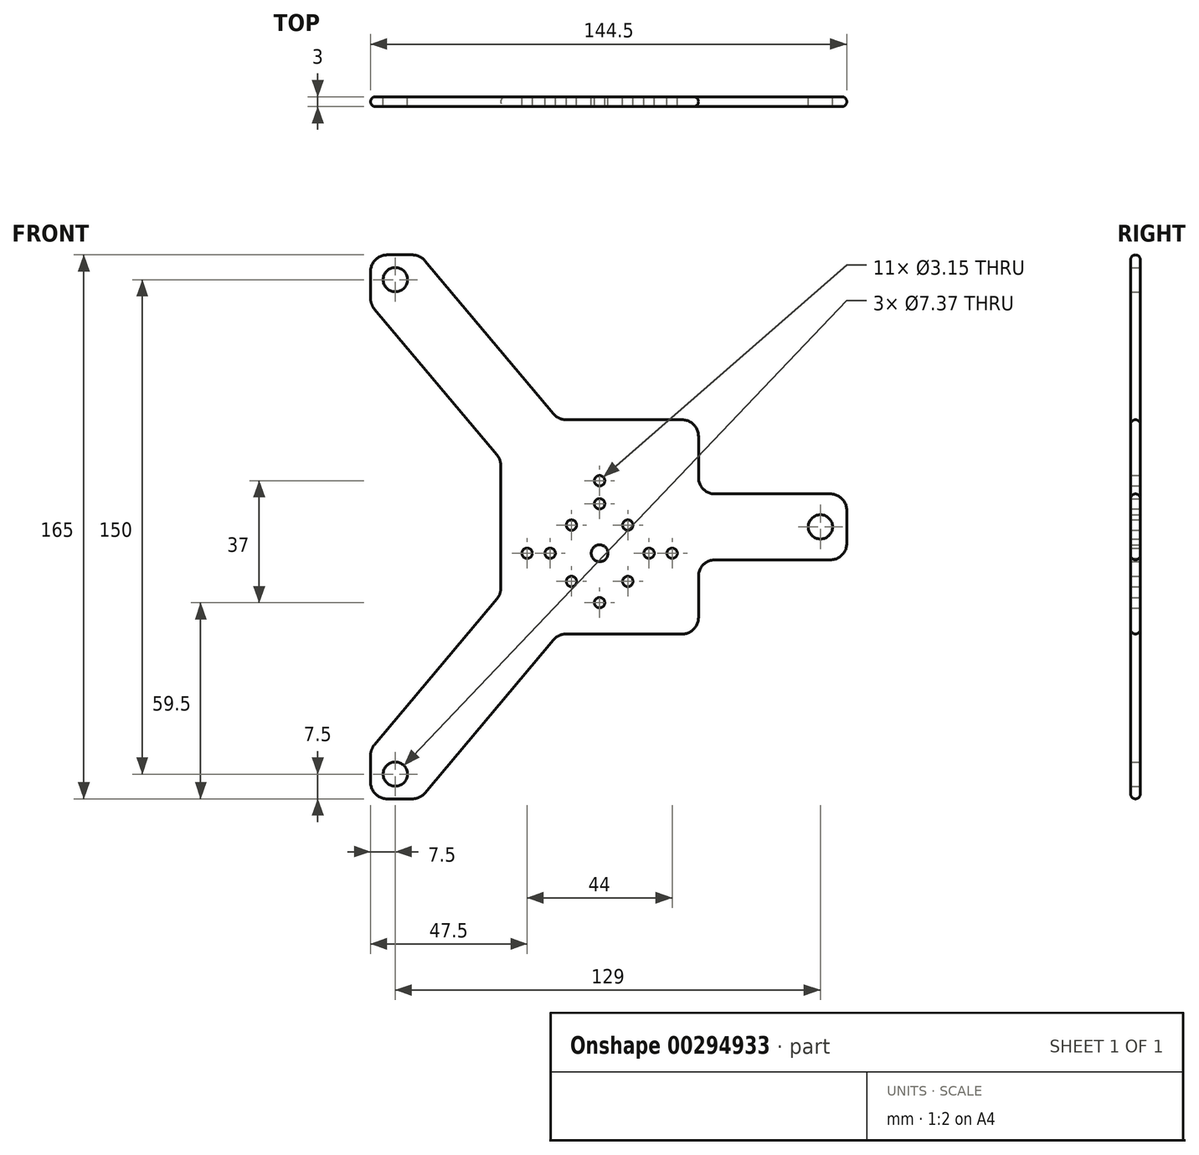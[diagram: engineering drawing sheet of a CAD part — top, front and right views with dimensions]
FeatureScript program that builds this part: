
annotation { "Feature Type Name" : "Feature", "Feature Type Description" : "" }
export const myFeature = defineFeature(function(context is Context, id is Id, definition is map)
    precondition{}
    {
        {
            var Q0;
            Q0=qCreatedBy(makeId("Front.planeOp"),FACE);
            var sketch = newSketch(context, id + "F0", { "sketchPlane" : qUnion([Q0])});
            skPoint(sketch, "E0.middle", {"position": v(0, 0) * mm});
            skCircle(sketch, "E1", {"center": v(0, -8) * mm, "radius": 2.55 * mm});
            skCircle(sketch, "E2", {"center": v(0, 7) * mm, "radius": 1.57 * mm});
            skCircle(sketch, "E3", {"center": v(0, 14) * mm, "radius": 1.57 * mm});
            skCircle(sketch, "E4", {"center": v(15, -8) * mm, "radius": 1.57 * mm});
            skCircle(sketch, "E5", {"center": v(22, -8) * mm, "radius": 1.57 * mm});
            skCircle(sketch, "E6", {"center": v(8.55, 0.55) * mm, "radius": 1.57 * mm});
            skCircle(sketch, "E7.MirrorC", {"center": v(-8.55, 0.55) * mm, "radius": 1.57 * mm});
            skCircle(sketch, "E8.MirrorC", {"center": v(-15, -8) * mm, "radius": 1.57 * mm});
            skCircle(sketch, "E9.MirrorC", {"center": v(-22, -8) * mm, "radius": 1.57 * mm});
            skCircle(sketch, "E10.MirrorC", {"center": v(8.55, -16.55) * mm, "radius": 1.57 * mm});
            skCircle(sketch, "E11.MirrorC", {"center": v(-8.55, -16.55) * mm, "radius": 1.57 * mm});
            skCircle(sketch, "E12.MirrorC", {"center": v(0, -23) * mm, "radius": 1.57 * mm});
            skCircle(sketch, "E13", {"center": v(-62, 75) * mm, "radius": 3.68 * mm});
            skCircle(sketch, "E14", {"center": v(-62, -75) * mm, "radius": 3.68 * mm});
            skLineSegment(sketch, "E15.bottom", {"start": v(-56.83, -82.5) * mm, "end": v(-64.5, -82.5) * mm});
            skLineSegment(sketch, "E15.top", {"start": v(-56.83, 82.5) * mm, "end": v(-64.5, 82.5) * mm});
            skLineSegment(sketch, "E15.left", {"start": v(75, -5) * mm, "end": v(75, 5) * mm});
            skLineSegment(sketch, "E15.right", {"start": v(-69.5, -77.5) * mm, "end": v(-69.5, -69.32) * mm});
            skLineSegment(sketch, "E16.bottom", {"start": v(25, -32.5) * mm, "end": v(-10.21, -32.5) * mm});
            skLineSegment(sketch, "E16.top", {"start": v(25, 32.5) * mm, "end": v(-10.21, 32.5) * mm});
            skLineSegment(sketch, "E16.left", {"start": v(30, -27.5) * mm, "end": v(30, -15) * mm});
            skLineSegment(sketch, "E16.right", {"start": v(-30, -18.6) * mm, "end": v(-30, 18.6) * mm});
            skCircle(sketch, "E17", {"center": v(67, 0) * mm, "radius": 3.68 * mm});
            skLineSegment(sketch, "E18", {"start": v(35, 10) * mm, "end": v(70, 10) * mm});
            skLineSegment(sketch, "E19.MirrorCS", {"start": v(35, -10) * mm, "end": v(70, -10) * mm});
            skLineSegment(sketch, "E20", {"start": v(-68.33, 66.1) * mm, "end": v(-31.17, 21.82) * mm});
            skLineSegment(sketch, "E21", {"start": v(-53, 80.71) * mm, "end": v(-14.04, 34.29) * mm});
            skLineSegment(sketch, "E22.MirrorCS", {"start": v(-68.33, -66.1) * mm, "end": v(-31.17, -21.82) * mm});
            skLineSegment(sketch, "E23.MirrorCS", {"start": v(-53, -80.71) * mm, "end": v(-14.04, -34.29) * mm});
            skLineSegment(sketch, "E24.trimOffspring", {"start": v(-69.5, 69.32) * mm, "end": v(-69.5, 77.5) * mm});
            skPoint(sketch, "E25.MirrorCS.start.orphan", {"position": v(-69.5, -67.5) * mm});
            skPoint(sketch, "E26.MirrorCS.end.orphan", {"position": v(-54.5, -82.5) * mm});
            skLineSegment(sketch, "E27.trimOffspring", {"start": v(30, 15) * mm, "end": v(30, 27.5) * mm});
            skPoint(sketch, "E28.orphan", {"position": v(30, 0) * mm});
            skPoint(sketch, "E29.orphan", {"position": v(69.5, 0) * mm});
            skPoint(sketch, "E30.visualSharp", {"position": v(-12.55, 32.5) * mm});
            skArc(sketch, "E30.filletArc", {"start": v(-14.04, 34.29) * mm, "mid": v(-12.33, 32.97) * mm, "end": v(-10.21, 32.5) * mm});
            skPoint(sketch, "E31.visualSharp", {"position": v(-30, 20.43) * mm});
            skArc(sketch, "E31.filletArc", {"start": v(-30, 18.6) * mm, "mid": v(-30.3, 20.32) * mm, "end": v(-31.17, 21.82) * mm});
            skPoint(sketch, "E32.visualSharp", {"position": v(-30, -20.43) * mm});
            skArc(sketch, "E32.filletArc", {"start": v(-31.17, -21.82) * mm, "mid": v(-30.3, -20.32) * mm, "end": v(-30, -18.6) * mm});
            skPoint(sketch, "E33.visualSharp", {"position": v(-12.55, -32.5) * mm});
            skArc(sketch, "E33.filletArc", {"start": v(-10.21, -32.5) * mm, "mid": v(-12.33, -32.97) * mm, "end": v(-14.04, -34.29) * mm});
            skPoint(sketch, "E34.visualSharp", {"position": v(30, -32.5) * mm});
            skArc(sketch, "E34.filletArc", {"start": v(25, -32.5) * mm, "mid": v(28.54, -31.04) * mm, "end": v(30, -27.5) * mm});
            skPoint(sketch, "E35.visualSharp", {"position": v(30, -10) * mm});
            skArc(sketch, "E35.filletArc", {"start": v(35, -10) * mm, "mid": v(31.46, -11.46) * mm, "end": v(30, -15) * mm});
            skPoint(sketch, "E36.visualSharp", {"position": v(30, 10) * mm});
            skArc(sketch, "E36.filletArc", {"start": v(30, 15) * mm, "mid": v(31.46, 11.46) * mm, "end": v(35, 10) * mm});
            skPoint(sketch, "E37.visualSharp", {"position": v(30, 32.5) * mm});
            skArc(sketch, "E37.filletArc", {"start": v(30, 27.5) * mm, "mid": v(28.54, 31.04) * mm, "end": v(25, 32.5) * mm});
            skPoint(sketch, "E38.visualSharp", {"position": v(75, 10) * mm});
            skArc(sketch, "E38.filletArc", {"start": v(75, 5) * mm, "mid": v(73.54, 8.54) * mm, "end": v(70, 10) * mm});
            skPoint(sketch, "E39.visualSharp", {"position": v(75, -10) * mm});
            skArc(sketch, "E39.filletArc", {"start": v(70, -10) * mm, "mid": v(73.54, -8.54) * mm, "end": v(75, -5) * mm});
            skArc(sketch, "E40.filletArc", {"start": v(-56.83, -82.5) * mm, "mid": v(-54.72, -82.03) * mm, "end": v(-53, -80.71) * mm});
            skPoint(sketch, "E41.visualSharp", {"position": v(-69.5, -82.5) * mm});
            skArc(sketch, "E41.filletArc", {"start": v(-69.5, -77.5) * mm, "mid": v(-68.04, -81.04) * mm, "end": v(-64.5, -82.5) * mm});
            skArc(sketch, "E42.filletArc", {"start": v(-68.33, -66.1) * mm, "mid": v(-69.2, -67.6) * mm, "end": v(-69.5, -69.32) * mm});
            skPoint(sketch, "E43.visualSharp", {"position": v(-69.5, 67.5) * mm});
            skArc(sketch, "E43.filletArc", {"start": v(-69.5, 69.32) * mm, "mid": v(-69.2, 67.6) * mm, "end": v(-68.33, 66.1) * mm});
            skPoint(sketch, "E44.visualSharp", {"position": v(-69.5, 82.5) * mm});
            skArc(sketch, "E44.filletArc", {"start": v(-64.5, 82.5) * mm, "mid": v(-68.04, 81.04) * mm, "end": v(-69.5, 77.5) * mm});
            skPoint(sketch, "E45.visualSharp", {"position": v(-54.5, 82.5) * mm});
            skArc(sketch, "E45.filletArc", {"start": v(-53, 80.71) * mm, "mid": v(-54.72, 82.03) * mm, "end": v(-56.83, 82.5) * mm});
            skSolve(sketch);
        }
        {
            var Q0;
            Q0=makeQuery(id+"F0.imprint","IMPRINT",FACE,{"disambiguationData":[TD([[makeQuery(id+"F0.imprint","IMPRINT",EDGE,{"derivedFrom":sQuery(id+"F0.wireOp",EDGE,"E1")}),-1.0]])]});
            extrude(context, id + "F1", {"entities" : qUnion([Q0]), "depth" : 3 * mm});
        }
        {
            var Q0;
            Q0=makeQuery(id+"F1.opExtrude","CAP_EDGE",EDGE,{"disambiguationData":[OSD([sQuery(id+"F0.wireOp",EDGE,"E21")])],"isStart":false});
            var Q1;
            Q1=makeQuery(id+"F1.opExtrude","CAP_EDGE",EDGE,{"disambiguationData":[OSD([sQuery(id+"F0.wireOp",EDGE,"E19.MirrorCS")])],"isStart":true});
            fillet(context, id + "F2", {"entities" : qUnion([Q0, Q1]), "radius" : 1.5 * mm, "tangentPropagation" : true, "allowEdgeOverflow" : false});
        }
    });
